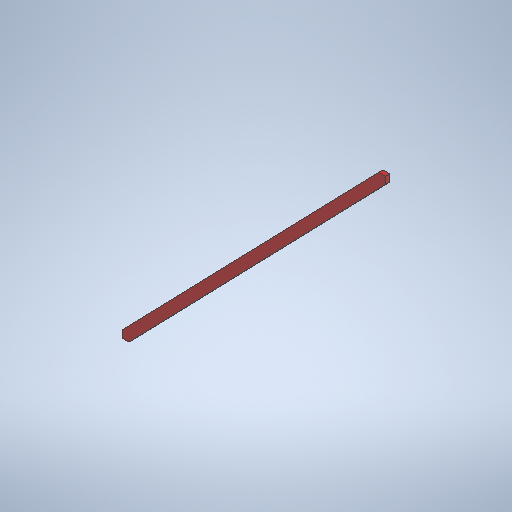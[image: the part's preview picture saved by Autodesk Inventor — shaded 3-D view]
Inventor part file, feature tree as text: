
AUTODESK INVENTOR PART (.ipt)
format: ipt  version: 2025.1 (Build 291241020, 241B)  size: 258,048 bytes
history: native  units: in
note: dims shown in document units (in); Inventor stores cm internally (conversion verified against a paired STEP export)
features: other x7, reference x4, plane x1, extrude x1, sketch x1
ambient origin geometry x8: Origin, YZ Plane, XZ Plane, XY Plane, X Axis, Y Axis, Z Axis, Center Point
bodies: Solid1 (feature_tree)
feature tree (14):
  plane  "Work Plane1"
  extrude  "Extrusion1"  [1 undecoded]
  sketch  "Sketch1"  dims[d2=1.5in d3=0.0in]
  reference  "Reference1"
  reference  "Reference2"
  reference  "Reference3"
  reference  "Reference4"
  other  "<userpath>\Documents\Tburn24\layer2\layer2.iam"
  other  "layer2.iam"
  other  "8'x2x4:4"
  other  "8'x2x4:5"
  other  "12'x2x4:2"
  other  "8'x2x4:1"
  other  "Finish1"
note: 1 required parameter value undecoded (feature->parameter linkage not recoverable at this tier; creation-order binding heuristic only, values carry confidence <= 0.55)
